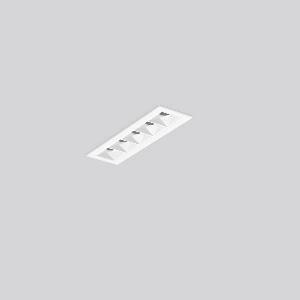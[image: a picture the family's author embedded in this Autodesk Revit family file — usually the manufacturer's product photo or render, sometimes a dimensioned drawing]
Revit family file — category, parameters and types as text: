
# Revit family: beamline_slim_641324_0025_9129
name_source: partatom
category: Lighting Fixtures
units: mm (PartAtom-declared; Revit-internal decimal feet)

## family parameters
Cut with Voids When Loaded = No
Host = Face
Light Source = No
Part Type = Normal
Room Calculation Point = No
Round Connector Dimension = Use Diameter
Shared = No

## types (1)
- BEAMLINE SLIM (1 x LED Modul 927, 940 lm, 2700)
    Apparent Load = 14 VA
    CIE Flux Codes = 100 100 100 100 100
    Color Rendering = 92
    Color Temperature = 2700
    Default Elevation = 1800 mm
    Description = Series: BEAMLINE SLIM
Minimalistic recessed ceiling luminaire for aesthetically sophisticated lighting. Housing: metal, powder-coated. Perfect heat management with an aluminium heat sink. LED light unit with MRS technology: Mini-Reflector-System made of metallised thermoplastic with prismatic white glare-suppressing frame for pleasant glare-free light (RUG < 10). Medium beam light distribution. Ceiling installation with spring system. Including separate LED converter with connecting cable 450 mm. 
Colour: traffic white, matt (RAL 9016)
Length: 155 mm
Width: 45 mm
Height: 1.5 mm
Cut-out length: 150 mm
Cut-out width: 40 mm
Recess height: 110 mm
Luminaire: recess height: 60 mm
Lamp: LED
Socket: without socket
Colour temperature: 2700K
Colour rendering index (CRI): 90
System power: 14 W
Rated luminous flux: 940 lm
Luminous efficiency: 67 lm/W
Control gear: Regulated power supply
Protection class: II
Type of protection: IP 20
    Height = 0 mm  [stored 0 ft]
    Lamp = 1 x LED Modul 927
    Lamp Light Flux = 940 lm
    Lamp count = 1
    Length = 155 mm
    Lifetime = 50000 h
    Luminous efficacy = 67 lm/W
    Manufacturer = RZB
    ModVariant = No
    Model = 641324.0025
    Mounting Place = Ceiling
    Mounting Type = Recessed
    Number of Poles = 1
    OnlyDefault = Yes
    Power Factor = 1
    Product Name = BEAMLINE SLIM
    Product group = Recessed LED linear luminaires
    ProductGroupID = 407
    Protection Class = Protection class II
    Protection Degree = IP 20
    RLX_Detail_Level = 1
    RLX_Emergency_Light_Flux = 0 lm
    RLX_Emergency_Type = 0
    RLX_Emergency_Type_DB = No
    RlxData = <blob elided: 10725 chars, md5=38f124bb>
    Socket = socket
    Standby Power = 0 W
    System Light Flux = 940 lm
    System Power = 14 W
    Type Comments = Product without accessories
    Type Image = 641323.0025.jpg
    URL = http://relux.com
    VarID = ---
    Voltage = 230 V
    Voltage Range = 220-240 V
    Weight = 0.00 kg
    Width = 45 mm

note: [stored X ft] marks values corroborated as IEEE doubles in the binary element streams (Revit-internal decimal feet)

## geometry (parser evidence)
native form markers: Sweep x9
no freeform markers — native parametric forms only
